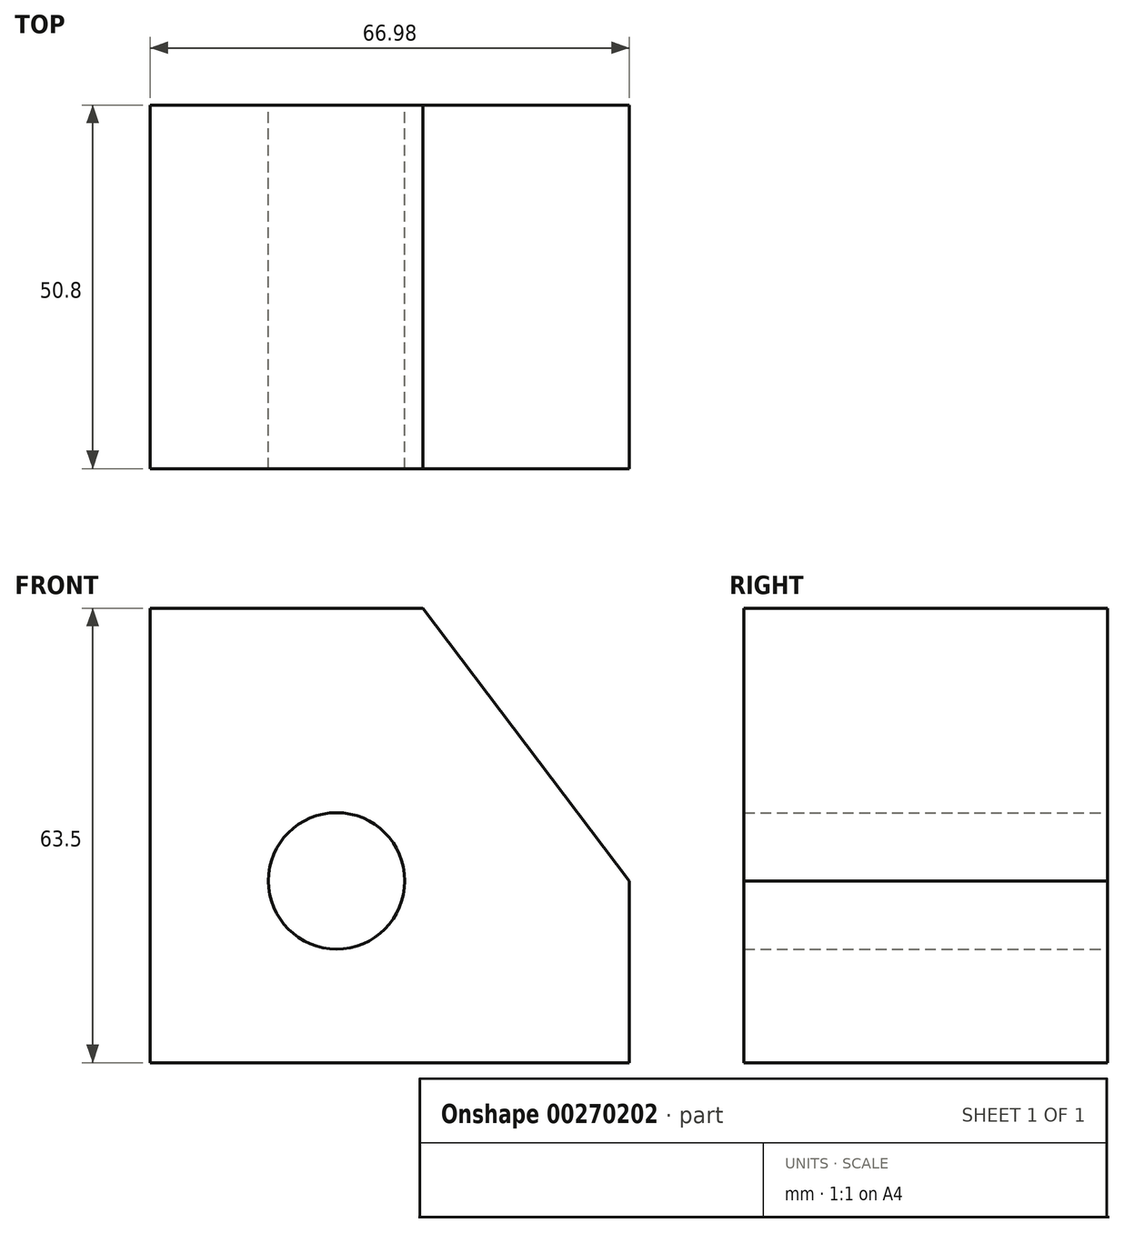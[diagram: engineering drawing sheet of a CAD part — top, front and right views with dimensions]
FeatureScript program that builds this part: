
annotation { "Feature Type Name" : "Feature", "Feature Type Description" : "" }
export const myFeature = defineFeature(function(context is Context, id is Id, definition is map)
    precondition{}
    {
        {
            var Q0;
            Q0=qCreatedBy(makeId("Front.planeOp"),FACE);
            var sketch = newSketch(context, id + "F0", { "sketchPlane" : qUnion([Q0])});
            skLineSegment(sketch, "E0", {"start": v(-30.48, 38.1) * mm, "end": v(-30.48, -25.4) * mm});
            skLineSegment(sketch, "E1", {"start": v(-30.48, -25.4) * mm, "end": v(45.72, -25.4) * mm});
            skLineSegment(sketch, "E2", {"start": v(-30.48, 38.1) * mm, "end": v(7.62, 38.1) * mm});
            skLineSegment(sketch, "E3", {"start": v(7.62, 38.1) * mm, "end": v(36.5, 0) * mm});
            skLineSegment(sketch, "E4", {"start": v(36.5, 0) * mm, "end": v(36.5, -25.4) * mm});
            skLineSegment(sketch, "E5", {"start": v(36.5, -25.4) * mm, "end": v(45.72, -25.4) * mm});
            skCircle(sketch, "E6", {"center": v(-4.41, 0) * mm, "radius": 0.67 * mm});
            skCircle(sketch, "E7", {"center": v(-4.41, 0) * mm, "radius": 9.53 * mm});
            skSolve(sketch);
        }
        {
            var Q0;
            Q0=makeQuery(id+"F0.imprint","IMPRINT",FACE,{"disambiguationData":[TD([[makeQuery(id+"F0.imprint","IMPRINT",EDGE,{"derivedFrom":sQuery(id+"F0.wireOp",EDGE,"E0")}),1.0]])]});
            extrude(context, id + "F1", {"entities" : qUnion([Q0]), "depth" : 50.8 * mm});
        }
    });
